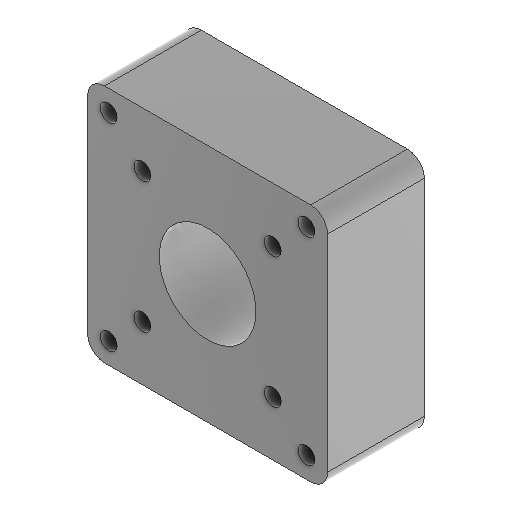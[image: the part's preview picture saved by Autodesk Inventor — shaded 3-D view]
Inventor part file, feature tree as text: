
AUTODESK INVENTOR PART (.ipt)
format: ipt  version: 2024.1 (Build 281209000, 209)  size: 150,016 bytes
history: native  units: mm
features: other x2, plane x1, extrude x1, sketch x1, reference x1
ambient origin geometry x8: Origin, YZ Plane, XZ Plane, XY Plane, X Axis, Y Axis, Z Axis, Center Point
bodies: Volumenkörper1 (feature_tree)
feature tree (6):
  plane  "Arbeitsebene1"
  extrude  "Extrusion1"  Depth=57.0mm
  sketch  "Skizze1"  dims[d0=57.0mm d1=57.0mm d2=4.0mm d3=47.0mm d4=47.0mm d5=4.0mm d6=4.0mm d7=4.0mm d8=4.0mm d9=23.0mm d10=0.0mm]
  reference  "Referenz1"
  other  "Assembly_Planktoscope_Uc2version.iam"
  other  "00_NEMA_17:1"
